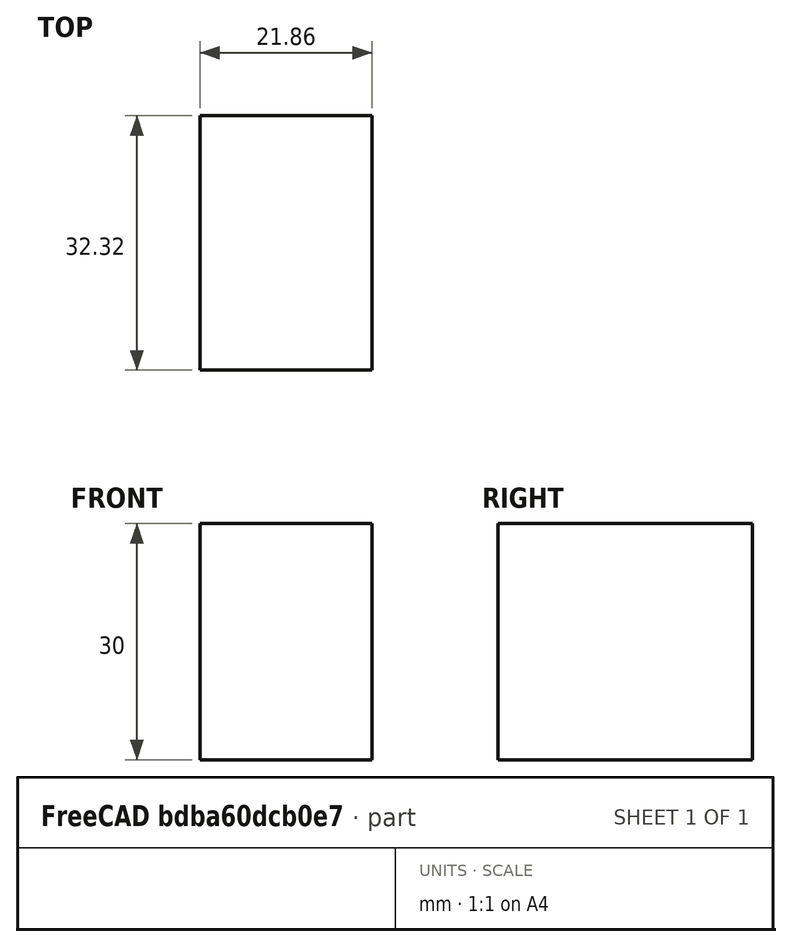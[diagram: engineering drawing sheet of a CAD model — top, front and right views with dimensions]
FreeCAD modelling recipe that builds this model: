
FCSTD DOCUMENT  (FreeCAD 0.16R)
Label: thrust_bearing_endstop_mount
License: All rights reserved
LicenseURL: http://en.wikipedia.org/wiki/All_rights_reserved
objects: Sketcher::SketchObject×2, PartDesign::Pad×1
note: 4 computed .brp shape members not serialized (recipe doc carries the construction recipe); baked Part::Feature solids carry a one-line shape summary decoded from their .brp

FEATURE [Sketcher::SketchObject] Sketch
  sketch-geometry (4):
    g0: LineSegment StartX=-10.1252 StartY=16.3479 StartZ=0 EndX=11.7283 EndY=16.3479 EndZ=0
    g1: LineSegment StartX=11.7283 StartY=16.3479 StartZ=0 EndX=11.7283 EndY=-15.9683 EndZ=0
    g2: LineSegment StartX=11.7283 StartY=-15.9683 StartZ=0 EndX=-10.1252 EndY=-15.9683 EndZ=0
    g3: LineSegment StartX=-10.1252 StartY=-15.9683 StartZ=0 EndX=-10.1252 EndY=16.3479 EndZ=0
  constraints (8):
    c: Coincident(g0,g1)
    c: Coincident(g1,g2)
    c: Coincident(g2,g3)
    c: Coincident(g3,g0)
    c: Horizontal(g0)
    c: Horizontal(g2)
    c: Vertical(g1)
    c: Vertical(g3)
FEATURE [PartDesign::Pad] Pad
  Length = 30
  Length2 = 100
  Sketch = -> Sketch
  Type = 0
FEATURE [Sketcher::SketchObject] Sketch001
  Placement = pos=(0,0,30) rot=(0,0,1;0rad)
  Support = -> Pad [Face6]
  sketch-geometry (2):
    g0: Circle CenterX=-5.25 CenterY=11 CenterZ=0 NormalX=0 NormalY=0 NormalZ=1 Radius=1.6
    g1: Circle CenterX=5.25 CenterY=-11 CenterZ=0 NormalX=0 NormalY=0 NormalZ=1 Radius=1.6
  constraints (5):
    c: Radius(g1) = 1.6
    c: Equal(g1,g0)
    c: DistanceX(g0,g1) = 10.5
    c: DistanceY(g1,g0) = 22
    c: Symmetric(g0,g1,g-1)
